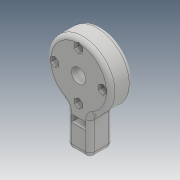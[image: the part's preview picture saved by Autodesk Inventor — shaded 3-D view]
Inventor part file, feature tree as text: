
AUTODESK INVENTOR PART (.ipt)
format: ipt  version: 2017 (Build 210142000, 142)  size: 255,488 bytes
history: native  units: mm
features: extrude x4, sketch x4, fillet x3, other x1
ambient origin geometry x8: Origin, YZ Plane, XZ Plane, XY Plane, X Axis, Y Axis, Z Axis, Center Point
bodies: Body1 (feature_tree)
feature tree (12):
  other  "Sólido1"
  extrude  "Extrusión1"  Depth=3.2mm
  extrude  "Extrusión2"  Depth=37.0mm
  extrude  "Extrusión3"  Depth=16.0mm TaperAngle=0.0deg
  fillet  "Empalme1"  Radius=16.0mm
  extrude  "Extrusión4"  Depth=10.0mm TaperAngle=0.0deg
  fillet  "Empalme2"  Radius=10.0mm
  fillet  "Empalme3"  Radius=5.0mm
  sketch  "Boceto1"  dims[d0=10.0mm d1=3.2mm]
  sketch  "Boceto2"  dims[d2=37.0mm d3=37.0mm]
  sketch  "Boceto3"  dims[d4=4.0mm d5=16.0mm d6=0.0mm d7=16.0mm]
  sketch  "Boceto4"  dims[d8=6.3mm d9=10.0mm d10=0.0mm d11=10.0mm d12=5.0mm d13=10.0mm d14=0.0mm d15=5.0mm d16=5.8mm d17=6.0mm d18=0.0mm d19=3.0mm d20=4.0mm]
